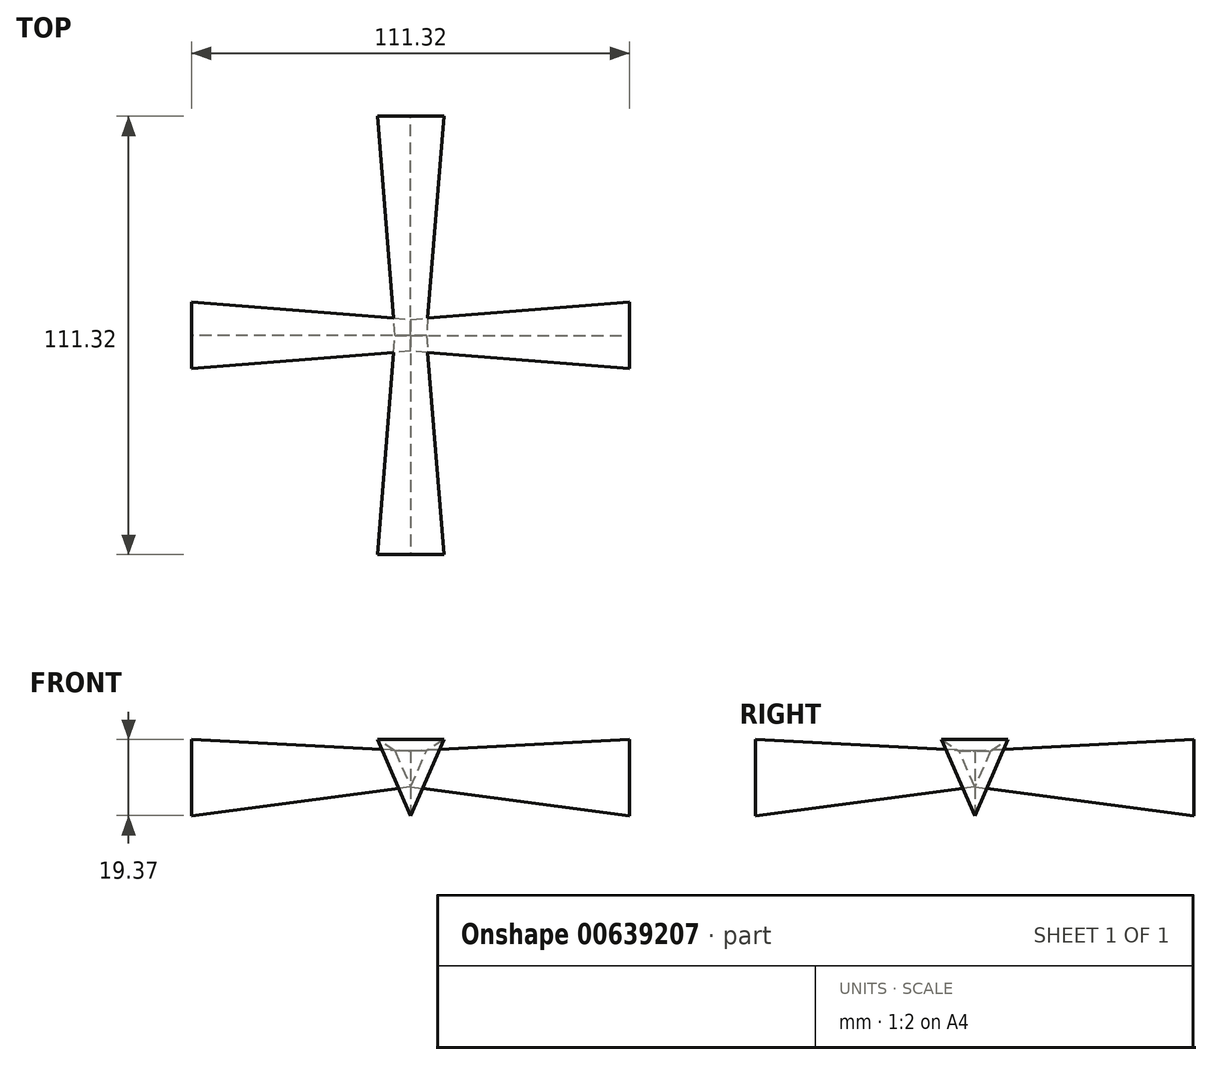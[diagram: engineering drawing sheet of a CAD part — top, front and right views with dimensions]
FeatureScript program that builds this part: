
annotation { "Feature Type Name" : "Feature", "Feature Type Description" : "" }
export const myFeature = defineFeature(function(context is Context, id is Id, definition is map)
    precondition{}
    {
        {
            var Q0;
            Q0=qCreatedBy(makeId("Front.planeOp"),FACE);
            var sketch = newSketch(context, id + "F0", { "sketchPlane" : qUnion([Q0])});
            skLineSegment(sketch, "E0", {"start": v(0, 0) * mm, "end": v(-8.75, 0) * mm, "construction": true});
            skLineSegment(sketch, "E1", {"start": v(0, 0) * mm, "end": v(0, 11) * mm, "construction": true});
            skLineSegment(sketch, "E2", {"start": v(-8.75, 11) * mm, "end": v(0, 11) * mm});
            skLineSegment(sketch, "E3", {"start": v(-11, 0) * mm, "end": v(-11, 3.61) * mm});
            skLineSegment(sketch, "E4", {"start": v(-11, 8.3) * mm, "end": v(-10.27, 7.7) * mm});
            skLineSegment(sketch, "E5", {"start": v(-10.27, 7.7) * mm, "end": v(-11, 7.23) * mm});
            skLineSegment(sketch, "E6", {"start": v(-11, 6.55) * mm, "end": v(-10.15, 6.01) * mm});
            skLineSegment(sketch, "E7", {"start": v(-10.15, 6.01) * mm, "end": v(-11, 5.42) * mm});
            skLineSegment(sketch, "E8", {"start": v(-11, 5.42) * mm, "end": v(-11, 4.68) * mm});
            skLineSegment(sketch, "E9", {"start": v(-11, 4.68) * mm, "end": v(-10.18, 4.14) * mm});
            skLineSegment(sketch, "E10", {"start": v(-10.18, 4.14) * mm, "end": v(-11, 3.61) * mm});
            skLineSegment(sketch, "E11.trimOffspring", {"start": v(-11, 4.68) * mm, "end": v(-11, 5.42) * mm});
            skLineSegment(sketch, "E12.trimOffspring", {"start": v(-11, 6.55) * mm, "end": v(-11, 7.23) * mm});
            skLineSegment(sketch, "E13.trimOffspring", {"start": v(-11, 8.3) * mm, "end": v(-11, 10) * mm});
            skLineSegment(sketch, "E14", {"start": v(-16.37, 26.42) * mm, "end": v(-15.47, 26.42) * mm});
            skFitSpline(sketch, "E15", {"points": [v(-15.47, 26.42) * mm, v(-10.61, 16.96) * mm, v(0, 14.4) * mm], "startDerivative": vector(2.8, -16.48) * mm, "endDerivative": vector(25.92, -1.74) * mm});
            skFitSpline(sketch, "E16", {"points": [v(0, 14.4) * mm, v(0, 11) * mm], "startDerivative": vector(0, -3.4) * mm, "endDerivative": vector(0, -3.4) * mm});
            skFitSpline(sketch, "E17", {"points": [v(-16.37, 26.42) * mm, v(-15.82, 16.9) * mm, v(-13.43, 12.56) * mm, v(-11, 10) * mm], "startDerivative": vector(-3.96, -16.59) * mm, "endDerivative": vector(10.58, -8.7) * mm});
            skLineSegment(sketch, "E18", {"start": v(-11, 0) * mm, "end": v(-8.75, 0) * mm});
            skLineSegment(sketch, "E19", {"start": v(-8.75, 11) * mm, "end": v(-8.75, 0) * mm});
            skSolve(sketch);
        }
        {
            var Q0;
            Q0=sQuery(id+"F0.wireOp",EDGE,"E14");
            var Q1;
            Q1=sQuery(id+"F0.wireOp",EDGE,"E17");
            var Q2;
            Q2=sQuery(id+"F0.wireOp",EDGE,"E15");
            var Q3;
            Q3=sQuery(id+"F0.wireOp",EDGE,"E2");
            var Q4;
            Q4=sQuery(id+"F0.wireOp",EDGE,"E19");
            var Q5;
            Q5=sQuery(id+"F0.wireOp",EDGE,"E13.trimOffspring");
            var Q6;
            Q6=sQuery(id+"F0.wireOp",EDGE,"E4");
            var Q7;
            Q7=sQuery(id+"F0.wireOp",EDGE,"E5");
            var Q8;
            Q8=sQuery(id+"F0.wireOp",EDGE,"E12.trimOffspring");
            var Q9;
            Q9=sQuery(id+"F0.wireOp",EDGE,"E6");
            var Q10;
            Q10=sQuery(id+"F0.wireOp",EDGE,"E7");
            var Q11;
            Q11=sQuery(id+"F0.wireOp",EDGE,"E11.trimOffspring");
            var Q12;
            Q12=sQuery(id+"F0.wireOp",EDGE,"E9");
            var Q13;
            Q13=sQuery(id+"F0.wireOp",EDGE,"E10");
            var Q14;
            Q14=sQuery(id+"F0.wireOp",EDGE,"E3");
            var Q15;
            Q15=sQuery(id+"F0.wireOp",EDGE,"E18");
            var Q16;
            Q16=sQuery(id+"F0.wireOp",EDGE,"E1");
            revolve(context, id + "F1", {"bodyType" : ToolBodyType.SURFACE, "surfaceEntities" : qUnion([Q0, Q1, Q2, Q3, Q4, Q5, Q6, Q7, Q8, Q9, Q10, Q11, Q12, Q13, Q14, Q15]), "axis" : qUnion([Q16]), "revolveType" : RevolveType.FULL});
        }
        {
            var Q0;
            Q0=qCreatedBy(makeId("Front.planeOp"),FACE);
            var sketch = newSketch(context, id + "F2", { "sketchPlane" : qUnion([Q0])});
            skLineSegment(sketch, "E20", {"start": v(0, 28.32) * mm, "end": v(4, 28.32) * mm});
            skLineSegment(sketch, "E21", {"start": v(4, 28.32) * mm, "end": v(0, 19.16) * mm});
            skLineSegment(sketch, "E22.MirrorCS", {"start": v(0, 28.32) * mm, "end": v(-4, 28.32) * mm});
            skLineSegment(sketch, "E23.MirrorCS", {"start": v(-4, 28.32) * mm, "end": v(0, 19.16) * mm});
            skSolve(sketch);
        }
        {
            var Q0;
            Q0=makeQuery(id+"F2.imprint","IMPRINT",FACE,{"disambiguationData":[TD([[makeQuery(id+"F2.imprint","IMPRINT",EDGE,{"derivedFrom":sQuery(id+"F2.wireOp",EDGE,"E20")}),-1.0]])]});
            extrude(context, id + "F3", {"entities" : qUnion([Q0]), "endBound" : BoundingType.THROUGH_ALL, "oppositeDirection" : true, "depth" : 25 * mm, "offsetDistance" : 25 * mm, "hasDraft" : true, "draftAngle" : 3 * degree});
        }
        {
            var Q0;
            Q0=makeQuery(id+"F3.opExtrude","SWEPT_BODY",BODY,{"disambiguationData":[OSD([sQuery(id+"F2.wireOp",EDGE,"E20"),sQuery(id+"F2.wireOp",EDGE,"E21"),sQuery(id+"F2.wireOp",EDGE,"E22.MirrorCS"),sQuery(id+"F2.wireOp",EDGE,"E23.MirrorCS")])]});
            var Q1;
            Q1=makeQuery(id+"F1.opRevolve","SWEPT_FACE",FACE,{"disambiguationData":[OSD([sQuery(id+"F0.wireOp",EDGE,"E13.trimOffspring")])]});
            circularPattern(context, id + "F4", {"entities" : qUnion([Q0]), "axis" : qUnion([Q1]), "angle" : 360 * degree, "instanceCount" : 4, "equalSpace" : true});
        }
    });
